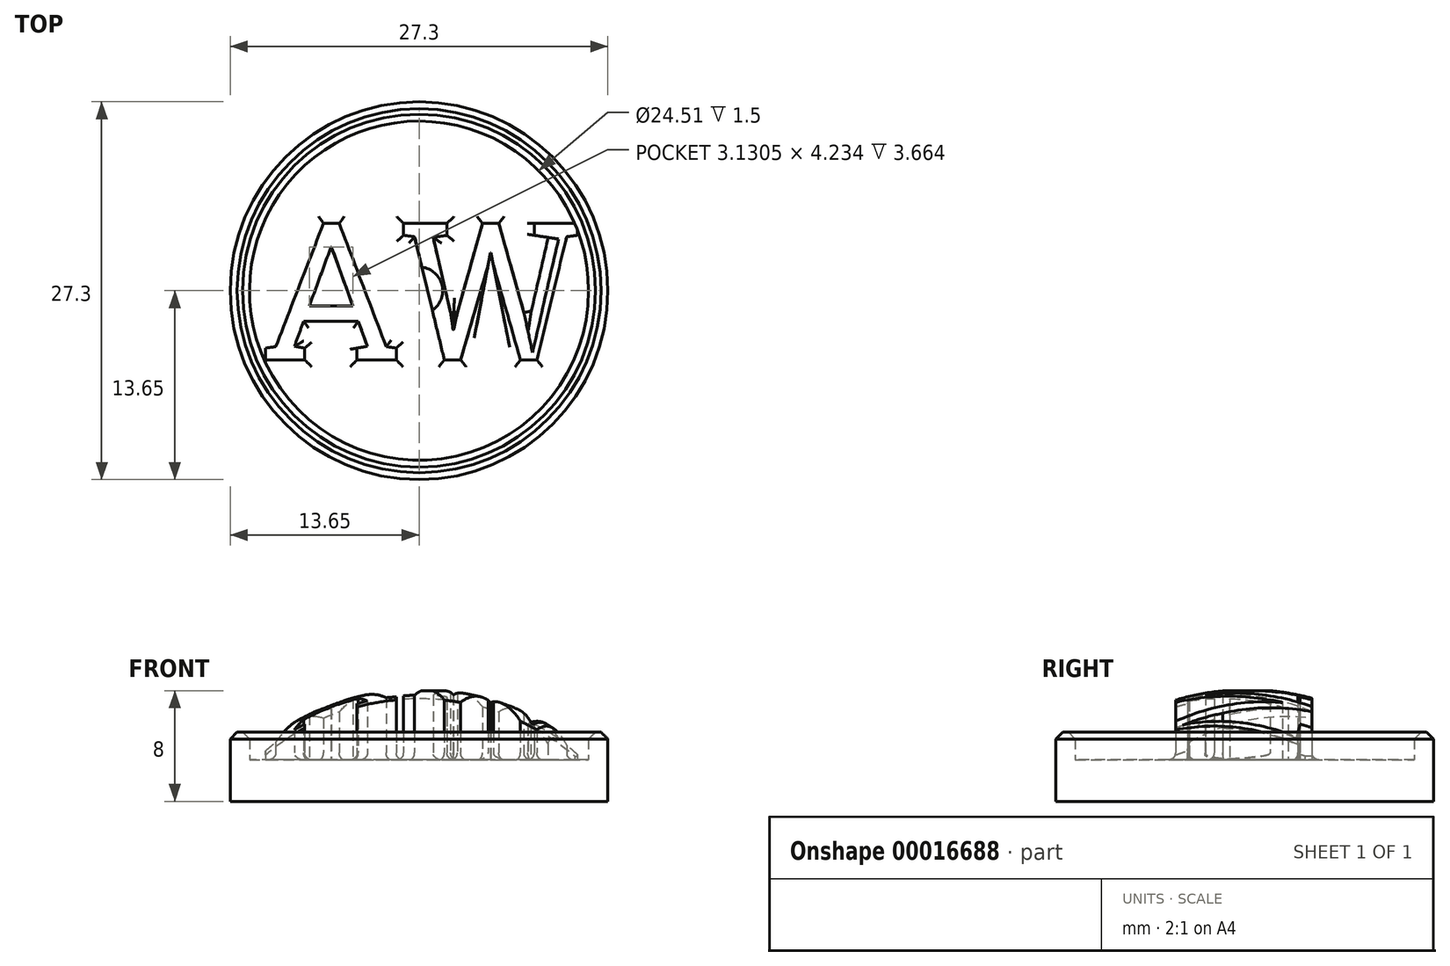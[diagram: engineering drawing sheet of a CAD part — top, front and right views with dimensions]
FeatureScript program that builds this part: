
annotation { "Feature Type Name" : "Feature", "Feature Type Description" : "" }
export const myFeature = defineFeature(function(context is Context, id is Id, definition is map)
    precondition{}
    {
        {
            var Q0;
            Q0=qCreatedBy(makeId("Top.planeOp"),FACE);
            var sketch = newSketch(context, id + "F0", { "sketchPlane" : qUnion([Q0])});
            skCircle(sketch, "E0", {"center": v(0, 0) * mm, "radius": 12.5 * mm});
            skText(sketch, "E1", { "text": "AW", "fontName": "RobotoSlab-Regular.ttf"});
            const initialGuessF0  = {"E1": [-0.01146, -0.005, 1, 0, 0.00999]};
            skSetInitialGuess(sketch, initialGuessF0);
            skSolve(sketch);
        }
        {
            var Q0;
            Q0=makeQuery(id+"F0.imprint","IMPRINT",FACE,{"disambiguationData":[TD([[makeQuery(id+"F0.imprint","IMPRINT",EDGE,{"derivedFrom":sQuery(id+"F0.wireOp",EDGE,"E1.sketch_text.stroke-0")}),-1.0]])]});
            var Q1;
            Q1=makeQuery(id+"F0.imprint","IMPRINT",FACE,{"disambiguationData":[TD([[makeQuery(id+"F0.imprint","IMPRINT",EDGE,{"derivedFrom":sQuery(id+"F0.wireOp",EDGE,"E1.sketch_text.stroke-20")}),-1.0]])]});
            var Q2;
            Q2=sQuery(id+"F0.wireOp",EDGE,"E0");
            extrude(context, id + "F1", {"entities" : qUnion([Q0, Q1]), "surfaceEntities" : qUnion([Q2]), "depth" : 5 * mm});
        }
        {
            var Q0;
            Q0=makeQuery(id+"F0.imprint","IMPRINT",FACE,{"disambiguationData":[TD([[makeQuery(id+"F0.imprint","IMPRINT",EDGE,{"derivedFrom":sQuery(id+"F0.wireOp",EDGE,"E0")}),1.0]])]});
            var Q1;
            Q1=makeQuery(id+"F0.imprint","IMPRINT",FACE,{"disambiguationData":[TD([[makeQuery(id+"F0.imprint","IMPRINT",EDGE,{"derivedFrom":sQuery(id+"F0.wireOp",EDGE,"E1.sketch_text.stroke-0")}),-1.0]])]});
            var Q2;
            Q2=makeQuery(id+"F0.imprint","IMPRINT",FACE,{"disambiguationData":[TD([[makeQuery(id+"F0.imprint","IMPRINT",EDGE,{"derivedFrom":sQuery(id+"F0.wireOp",EDGE,"E1.sketch_text.stroke-16")}),1.0]])]});
            var Q3;
            Q3=makeQuery(id+"F0.imprint","IMPRINT",FACE,{"disambiguationData":[TD([[makeQuery(id+"F0.imprint","IMPRINT",EDGE,{"derivedFrom":sQuery(id+"F0.wireOp",EDGE,"E1.sketch_text.stroke-20")}),-1.0]])]});
            extrude(context, id + "F2", {"entities" : qUnion([Q0, Q1, Q2, Q3]), "operationType" : NewBodyOperationType.ADD, "oppositeDirection" : true, "depth" : 3 * mm});
        }
        {
            var Q0;
            Q0=qCreatedBy(makeId("Right.planeOp"),FACE);
            var sketch = newSketch(context, id + "F3", { "sketchPlane" : qUnion([Q0])});
            skArc(sketch, "E2", {"start": v(12.52, 0) * mm, "mid": v(0.3, 5.06) * mm, "end": v(-11.93, 0) * mm});
            skLineSegment(sketch, "E3", {"start": v(12.52, 0) * mm, "end": v(12.52, 8.46) * mm});
            skLineSegment(sketch, "E4", {"start": v(0, 8.46) * mm, "end": v(0, 5.06) * mm});
            skLineSegment(sketch, "E5", {"start": v(12.52, 8.46) * mm, "end": v(0, 8.46) * mm});
            skSolve(sketch);
        }
        {
            var Q0;
            Q0 = qSketchRegion(id + "F3", true);
            var Q1;
            Q1=sQuery(id+"F3.wireOp",EDGE,"E4");
            revolve(context, id + "F4", {"operationType" : NewBodyOperationType.REMOVE, "entities" : qUnion([Q0]), "axis" : qUnion([Q1]), "revolveType" : RevolveType.FULL, "oppositeDirection" : true});
        }
        {
            var Q0;
            Q0=makeQuery(id+"F1.opExtrude","CAP_EDGE",EDGE,{"disambiguationData":[OSD([sQuery(id+"F0.wireOp",EDGE,"E1.sketch_text.stroke-3")])],"isStart":true});
            var Q1;
            Q1=makeQuery(id+"F1.opExtrude","CAP_EDGE",EDGE,{"disambiguationData":[OSD([sQuery(id+"F0.wireOp",EDGE,"E1.sketch_text.stroke-2")])],"isStart":true});
            var Q2;
            Q2=makeQuery(id+"F1.opExtrude","CAP_EDGE",EDGE,{"disambiguationData":[OSD([sQuery(id+"F0.wireOp",EDGE,"E1.sketch_text.stroke-1")])],"isStart":true});
            var Q3;
            Q3=makeQuery(id+"F1.opExtrude","CAP_EDGE",EDGE,{"disambiguationData":[OSD([sQuery(id+"F0.wireOp",EDGE,"E1.sketch_text.stroke-4")])],"isStart":true});
            var Q4;
            Q4=makeQuery(id+"F1.opExtrude","CAP_EDGE",EDGE,{"disambiguationData":[OSD([sQuery(id+"F0.wireOp",EDGE,"E1.sketch_text.stroke-5")])],"isStart":true});
            var Q5;
            Q5=makeQuery(id+"F1.opExtrude","CAP_EDGE",EDGE,{"disambiguationData":[OSD([sQuery(id+"F0.wireOp",EDGE,"E1.sketch_text.stroke-6")])],"isStart":true});
            var Q6;
            Q6=makeQuery(id+"F1.opExtrude","CAP_EDGE",EDGE,{"disambiguationData":[OSD([sQuery(id+"F0.wireOp",EDGE,"E1.sketch_text.stroke-14")])],"isStart":true});
            var Q7;
            Q7=makeQuery(id+"F1.opExtrude","CAP_EDGE",EDGE,{"disambiguationData":[OSD([sQuery(id+"F0.wireOp",EDGE,"E1.sketch_text.stroke-48")])],"isStart":true});
            var Q8;
            Q8=makeQuery(id+"F1.opExtrude","CAP_EDGE",EDGE,{"disambiguationData":[OSD([sQuery(id+"F0.wireOp",EDGE,"E1.sketch_text.stroke-47")])],"isStart":true});
            var Q9;
            Q9=makeQuery(id+"F1.opExtrude","CAP_EDGE",EDGE,{"disambiguationData":[OSD([sQuery(id+"F0.wireOp",EDGE,"E1.sketch_text.stroke-17")])],"isStart":true});
            var Q10;
            Q10=makeQuery(id+"F1.opExtrude","CAP_EDGE",EDGE,{"disambiguationData":[OSD([sQuery(id+"F0.wireOp",EDGE,"E1.sketch_text.stroke-10")])],"isStart":true});
            var Q11;
            Q11=makeQuery(id+"F1.opExtrude","CAP_EDGE",EDGE,{"disambiguationData":[OSD([sQuery(id+"F0.wireOp",EDGE,"E1.sketch_text.stroke-9")])],"isStart":true});
            var Q12;
            Q12=makeQuery(id+"F1.opExtrude","CAP_EDGE",EDGE,{"disambiguationData":[OSD([sQuery(id+"F0.wireOp",EDGE,"E1.sketch_text.stroke-7")])],"isStart":true});
            var Q13;
            Q13=makeQuery(id+"F1.opExtrude","CAP_EDGE",EDGE,{"disambiguationData":[OSD([sQuery(id+"F0.wireOp",EDGE,"E1.sketch_text.stroke-11")])],"isStart":true});
            var Q14;
            Q14=makeQuery(id+"F1.opExtrude","CAP_EDGE",EDGE,{"disambiguationData":[OSD([sQuery(id+"F0.wireOp",EDGE,"E1.sketch_text.stroke-13")])],"isStart":true});
            var Q15;
            Q15=makeQuery(id+"F1.opExtrude","CAP_EDGE",EDGE,{"disambiguationData":[OSD([sQuery(id+"F0.wireOp",EDGE,"E1.sketch_text.stroke-12")])],"isStart":true});
            var Q16;
            Q16=makeQuery(id+"F1.opExtrude","CAP_EDGE",EDGE,{"disambiguationData":[OSD([sQuery(id+"F0.wireOp",EDGE,"E1.sketch_text.stroke-19")])],"isStart":true});
            var Q17;
            Q17=makeQuery(id+"F1.opExtrude","CAP_EDGE",EDGE,{"disambiguationData":[OSD([sQuery(id+"F0.wireOp",EDGE,"E1.sketch_text.stroke-16")])],"isStart":true});
            var Q18;
            Q18=makeQuery(id+"F1.opExtrude","CAP_EDGE",EDGE,{"disambiguationData":[OSD([sQuery(id+"F0.wireOp",EDGE,"E1.sketch_text.stroke-49")])],"isStart":true});
            var Q19;
            Q19=makeQuery(id+"F1.opExtrude","CAP_EDGE",EDGE,{"disambiguationData":[OSD([sQuery(id+"F0.wireOp",EDGE,"E1.sketch_text.stroke-20")])],"isStart":true});
            var Q20;
            Q20=makeQuery(id+"F1.opExtrude","CAP_EDGE",EDGE,{"disambiguationData":[OSD([sQuery(id+"F0.wireOp",EDGE,"E1.sketch_text.stroke-21")])],"isStart":true});
            var Q21;
            Q21=makeQuery(id+"F1.opExtrude","CAP_EDGE",EDGE,{"disambiguationData":[OSD([sQuery(id+"F0.wireOp",EDGE,"E1.sketch_text.stroke-25")])],"isStart":true});
            var Q22;
            Q22=makeQuery(id+"F1.opExtrude","CAP_EDGE",EDGE,{"disambiguationData":[OSD([sQuery(id+"F0.wireOp",EDGE,"E1.sketch_text.stroke-45")])],"isStart":true});
            var Q23;
            Q23=makeQuery(id+"F1.opExtrude","CAP_EDGE",EDGE,{"disambiguationData":[OSD([sQuery(id+"F0.wireOp",EDGE,"E1.sketch_text.stroke-46")])],"isStart":true});
            var Q24;
            Q24=makeQuery(id+"F1.opExtrude","CAP_EDGE",EDGE,{"disambiguationData":[OSD([sQuery(id+"F0.wireOp",EDGE,"E1.sketch_text.stroke-44")])],"isStart":true});
            var Q25;
            Q25=makeQuery(id+"F1.opExtrude","CAP_EDGE",EDGE,{"disambiguationData":[OSD([sQuery(id+"F0.wireOp",EDGE,"E1.sketch_text.stroke-43")])],"isStart":true});
            var Q26;
            Q26=makeQuery(id+"F1.opExtrude","CAP_EDGE",EDGE,{"disambiguationData":[OSD([sQuery(id+"F0.wireOp",EDGE,"E1.sketch_text.stroke-39")])],"isStart":true});
            var Q27;
            Q27=makeQuery(id+"F1.opExtrude","CAP_EDGE",EDGE,{"disambiguationData":[OSD([sQuery(id+"F0.wireOp",EDGE,"E1.sketch_text.stroke-38")])],"isStart":true});
            var Q28;
            Q28=makeQuery(id+"F1.opExtrude","CAP_EDGE",EDGE,{"disambiguationData":[OSD([sQuery(id+"F0.wireOp",EDGE,"E1.sketch_text.stroke-37")])],"isStart":true});
            var Q29;
            Q29=makeQuery(id+"F4.boolean.opBoolean","INTERSECT",EDGE,{"derivedFrom":[makeQuery(id+"F1.opExtrude","SWEPT_FACE",FACE,{"disambiguationData":[OSD([sQuery(id+"F0.wireOp",EDGE,"E1.sketch_text.stroke-31")])]}),makeQuery(id+"F4.opRevolve","SWEPT_FACE",FACE,{"disambiguationData":[OSD([sQuery(id+"F3.wireOp",EDGE,"E2")])]})]});
            var Q30;
            Q30=makeQuery(id+"F1.opExtrude","CAP_EDGE",EDGE,{"disambiguationData":[OSD([sQuery(id+"F0.wireOp",EDGE,"E1.sketch_text.stroke-27")])],"isStart":true});
            var Q31;
            Q31=makeQuery(id+"F1.opExtrude","CAP_EDGE",EDGE,{"disambiguationData":[OSD([sQuery(id+"F0.wireOp",EDGE,"E1.sketch_text.stroke-26")])],"isStart":true});
            var Q32;
            Q32=makeQuery(id+"F1.opExtrude","CAP_EDGE",EDGE,{"disambiguationData":[OSD([sQuery(id+"F0.wireOp",EDGE,"E1.sketch_text.stroke-33")])],"isStart":true});
            fillet(context, id + "F5", {"entities" : qUnion([Q0, Q1, Q2, Q3, Q4, Q5, Q6, Q7, Q8, Q9, Q10, Q11, Q12, Q13, Q14, Q15, Q16, Q17, Q18, Q19, Q20, Q21, Q22, Q23, Q24, Q25, Q26, Q27, Q28, Q29, Q30, Q31, Q32]), "radius" : 0.5 * mm, "tangentPropagation" : true, "allowEdgeOverflow" : false});
        }
        {
            var Q0;
            Q0=qCreatedBy(makeId("Top.planeOp"),FACE);
            var sketch = newSketch(context, id + "F6", { "sketchPlane" : qUnion([Q0])});
            skCircle(sketch, "E6", {"center": v(0, 0) * mm, "radius": 13.65 * mm});
            skCircle(sketch, "E7", {"center": v(0, 0) * mm, "radius": 12.25 * mm});
            skSolve(sketch);
        }
        {
            var Q0;
            Q0 = qSketchRegion(id + "F6", true);
            extrude(context, id + "F7", {"entities" : qUnion([Q0]), "depth" : 2 * mm});
        }
        {
            var Q0;
            Q0 = qSketchRegion(id + "F6", true);
            extrude(context, id + "F8", {"entities" : qUnion([Q0]), "operationType" : NewBodyOperationType.ADD, "oppositeDirection" : true, "depth" : 3 * mm});
        }
        {
            var Q0;
            Q0=makeQuery(id+"F7.opExtrude","CAP_EDGE",EDGE,{"disambiguationData":[OSD([sQuery(id+"F6.wireOp",EDGE,"E6")])],"isStart":false});
            var Q1;
            Q1=makeQuery(id+"F7.opExtrude","CAP_EDGE",EDGE,{"disambiguationData":[OSD([sQuery(id+"F6.wireOp",EDGE,"E7")])],"isStart":false});
            chamfer(context, id + "F9", {"entities" : qUnion([Q0, Q1]), "width" : 0.5 * mm, "tangentPropagation" : true});
        }
    });
